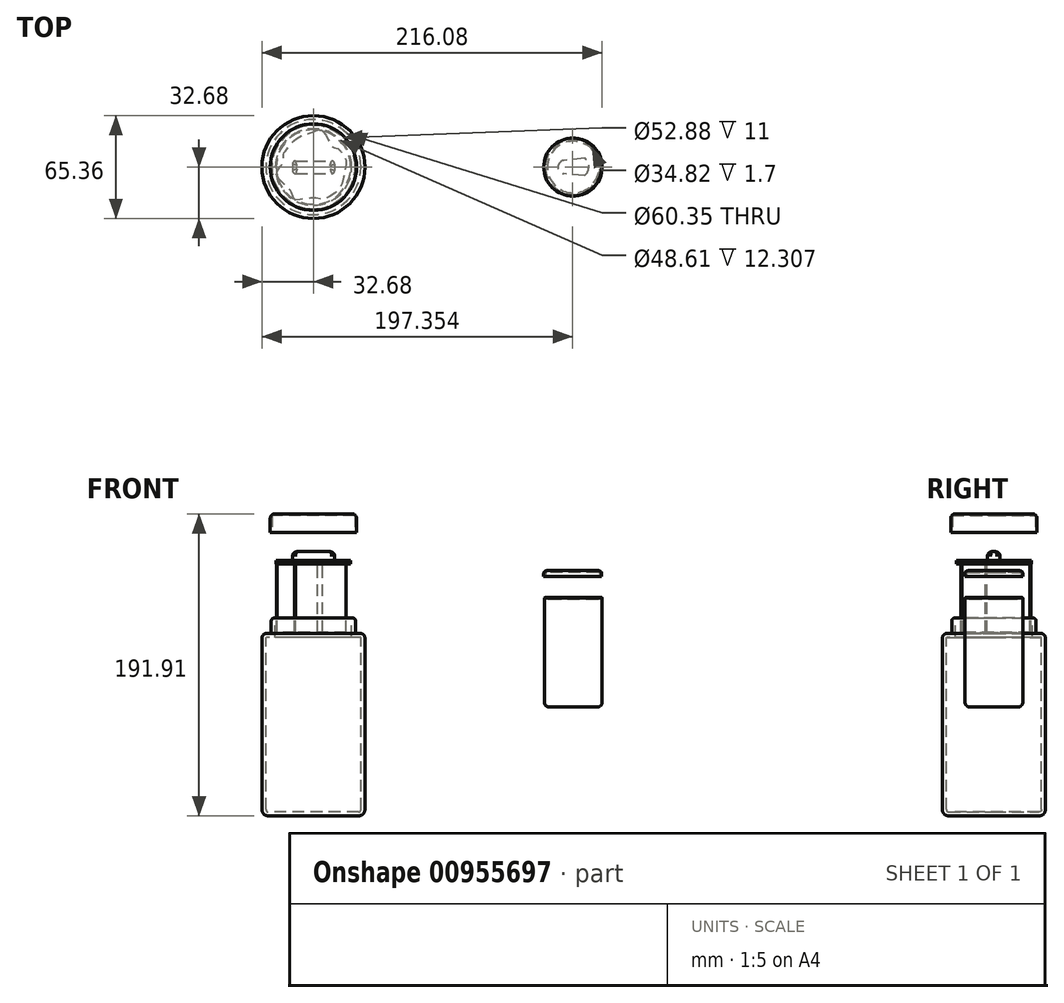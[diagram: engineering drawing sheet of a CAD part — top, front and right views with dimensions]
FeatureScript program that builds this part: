
annotation { "Feature Type Name" : "Feature", "Feature Type Description" : "" }
export const myFeature = defineFeature(function(context is Context, id is Id, definition is map)
    precondition{}
    {
        {
            var Q0;
            Q0=qCreatedBy(makeId("Front.planeOp"),FACE);
            var sketch = newSketch(context, id + "F0", { "sketchPlane" : qUnion([Q0])});
            skLineSegment(sketch, "E0", {"start": v(0, 62.51) * mm, "end": v(0, -116.4) * mm});
            skLineSegment(sketch, "E1", {"start": v(0, 58.07) * mm, "end": v(24.8, 58.07) * mm});
            skLineSegment(sketch, "E2", {"start": v(26.8, 56.07) * mm, "end": v(26.8, 48.27) * mm});
            skLineSegment(sketch, "E3", {"start": v(26.8, 48.27) * mm, "end": v(29.68, 48.27) * mm});
            skLineSegment(sketch, "E4", {"start": v(32.68, 45.27) * mm, "end": v(32.68, -63.64) * mm});
            skLineSegment(sketch, "E5", {"start": v(28.68, -67.64) * mm, "end": v(0, -67.64) * mm});
            skPoint(sketch, "E6.visualSharp", {"position": v(32.68, 48.27) * mm});
            skArc(sketch, "E6.filletArc", {"start": v(32.68, 45.27) * mm, "mid": v(31.8, 47.39) * mm, "end": v(29.68, 48.27) * mm});
            skPoint(sketch, "E7.visualSharp", {"position": v(32.68, -67.64) * mm});
            skArc(sketch, "E7.filletArc", {"start": v(28.68, -67.64) * mm, "mid": v(31.5, -66.47) * mm, "end": v(32.68, -63.64) * mm});
            skPoint(sketch, "E8.visualSharp", {"position": v(26.8, 58.07) * mm});
            skArc(sketch, "E8.filletArc", {"start": v(26.8, 56.07) * mm, "mid": v(26.22, 57.49) * mm, "end": v(24.8, 58.07) * mm});
            skSolve(sketch);
        }
        {
            var Q0;
            {var subQ0=sQuery(id+"F0.wireOp",EDGE,"E1");Q0=makeQuery(id+"F0.imprint","IMPRINT",FACE,{"disambiguationData":[TD([[makeQuery(id+"F0.imprint","IMPRINT",EDGE,{"derivedFrom":subQ0}),-1.0]])]});}
            var Q1;
            Q1=sQuery(id+"F0.wireOp",EDGE,"E0");
            revolve(context, id + "F1", {"surfaceOperationType" : NewSurfaceOperationType.NEW, "entities" : qUnion([Q0]), "axis" : qUnion([Q1]), "revolveType" : RevolveType.FULL});
        }
        {
            var Q0;
            Q0=makeQuery(id+"F1.opRevolve","SWEPT_FACE",FACE,{"disambiguationData":[OSD([sQuery(id+"F0.wireOp",EDGE,"E1")])]});
            shell(context, id + "F2", {"entities" : qUnion([Q0]), "thickness" : 2.5 * mm});
        }
        {
            var Q0;
            Q0=makeQuery(id+"F1.opRevolve","SWEPT_FACE",FACE,{"disambiguationData":[OSD([sQuery(id+"F0.wireOp",EDGE,"E3")])]});
            cPlane(context, id + "F3", {"entities" : qUnion([Q0]), "cplaneType" : CPlaneType.OFFSET, "offset" : 64 * mm, "width" : 150 * mm, "height" : 150 * mm});
        }
        {
            var Q0;
            Q0=qCreatedBy(id+"F3.planeOp",FACE);
            var sketch = newSketch(context, id + "F4", { "sketchPlane" : qUnion([Q0])});
            skCircle(sketch, "E9", {"center": v(0, 0) * mm, "radius": 27.44 * mm});
            skSolve(sketch);
        }
        {
            var Q0;
            Q0=makeQuery(id+"F4.imprint","IMPRINT",FACE,{"disambiguationData":[TD([[makeQuery(id+"F4.imprint","IMPRINT",EDGE,{"derivedFrom":sQuery(id+"F4.wireOp",EDGE,"E9")}),1.0]])]});
            extrude(context, id + "F5", {"entities" : qUnion([Q0]), "depth" : 12 * mm, "offsetDistance" : 25 * mm});
        }
        {
            var Q0;
            Q0=makeQuery(id+"F5.opExtrude","CAP_FACE",FACE,{"disambiguationData":[OSD([sQuery(id+"F4.wireOp",EDGE,"E9")])],"isStart":true});
            shell(context, id + "F6", {"entities" : qUnion([Q0]), "thickness" : 1 * mm});
        }
        {
            var Q0;
            Q0=qCreatedBy(id+"F3.planeOp",FACE);
            cPlane(context, id + "F7", {"entities" : qUnion([Q0]), "cplaneType" : CPlaneType.OFFSET, "offset" : 20 * mm, "oppositeDirection" : true, "width" : 150 * mm, "height" : 150 * mm});
        }
        {
            var Q0;
            Q0=qCreatedBy(id+"F7.planeOp",FACE);
            var sketch = newSketch(context, id + "F8", { "sketchPlane" : qUnion([Q0])});
            skCircle(sketch, "E10", {"center": v(0, 0) * mm, "radius": 23.67 * mm});
            skSolve(sketch);
        }
        {
            var Q0;
            Q0=makeQuery(id+"F8.imprint","IMPRINT",FACE,{"disambiguationData":[TD([[makeQuery(id+"F8.imprint","IMPRINT",EDGE,{"derivedFrom":sQuery(id+"F8.wireOp",EDGE,"E10")}),1.0]])]});
            extrude(context, id + "F9", {"entities" : qUnion([Q0]), "depth" : 2.4 * mm, "offsetDistance" : 25 * mm});
        }
        {
            var Q0;
            Q0=makeQuery(id+"F9.opExtrude","CAP_FACE",FACE,{"disambiguationData":[OSD([sQuery(id+"F8.wireOp",EDGE,"E10")])],"isStart":false});
            var sketch = newSketch(context, id + "F10", { "sketchPlane" : qUnion([Q0])});
            skLineSegment(sketch, "E11.bottom", {"start": v(-11.34, 3.9) * mm, "end": v(11.52, 3.9) * mm});
            skLineSegment(sketch, "E11.top", {"start": v(-11.34, -4.08) * mm, "end": v(11.52, -4.08) * mm});
            skLineSegment(sketch, "E11.left", {"start": v(-13.34, 1.9) * mm, "end": v(-13.34, -2.08) * mm});
            skLineSegment(sketch, "E11.right", {"start": v(13.52, 1.9) * mm, "end": v(13.52, -2.08) * mm});
            skPoint(sketch, "E12.visualSharp", {"position": v(-13.34, -4.08) * mm});
            skArc(sketch, "E12.filletArc", {"start": v(-13.34, -2.08) * mm, "mid": v(-12.75, -3.5) * mm, "end": v(-11.34, -4.08) * mm});
            skPoint(sketch, "E13.visualSharp", {"position": v(13.52, 3.9) * mm});
            skArc(sketch, "E13.filletArc", {"start": v(13.52, 1.9) * mm, "mid": v(12.93, 3.32) * mm, "end": v(11.52, 3.9) * mm});
            skPoint(sketch, "E14.visualSharp", {"position": v(13.52, -4.08) * mm});
            skArc(sketch, "E14.filletArc", {"start": v(11.52, -4.08) * mm, "mid": v(12.93, -3.5) * mm, "end": v(13.52, -2.08) * mm});
            skPoint(sketch, "E15.visualSharp", {"position": v(-13.34, 3.9) * mm});
            skArc(sketch, "E15.filletArc", {"start": v(-11.34, 3.9) * mm, "mid": v(-12.75, 3.32) * mm, "end": v(-13.34, 1.9) * mm});
            skSolve(sketch);
        }
        {
            var Q0;
            Q0=makeQuery(id+"F10.imprint","IMPRINT",FACE,{"disambiguationData":[TD([[makeQuery(id+"F10.imprint","IMPRINT",EDGE,{"derivedFrom":sQuery(id+"F10.wireOp",EDGE,"E11.bottom")}),-1.0]])]});
            extrude(context, id + "F11", {"entities" : qUnion([Q0]), "operationType" : NewBodyOperationType.ADD, "depth" : 5.5 * mm, "offsetDistance" : 25 * mm});
        }
        {
            var Q0;
            Q0=makeQuery(id+"F11.opExtrude","CAP_EDGE",EDGE,{"disambiguationData":[OSD([sQuery(id+"F10.wireOp",EDGE,"E11.top")])],"isStart":false});
            var Q1;
            Q1=makeQuery(id+"F11.opExtrude","CAP_EDGE",EDGE,{"disambiguationData":[OSD([sQuery(id+"F10.wireOp",EDGE,"E11.bottom")])],"isStart":false});
            var Q2;
            Q2=makeQuery(id+"F11.opExtrude","CAP_EDGE",EDGE,{"disambiguationData":[OSD([sQuery(id+"F10.wireOp",EDGE,"E11.right")])],"isStart":false});
            var Q3;
            Q3=makeQuery(id+"F11.opExtrude","CAP_EDGE",EDGE,{"disambiguationData":[OSD([sQuery(id+"F10.wireOp",EDGE,"E14.filletArc")])],"isStart":false});
            var Q4;
            Q4=makeQuery(id+"F11.opExtrude","CAP_EDGE",EDGE,{"disambiguationData":[OSD([sQuery(id+"F10.wireOp",EDGE,"E12.filletArc")])],"isStart":false});
            var Q5;
            Q5=makeQuery(id+"F11.opExtrude","CAP_EDGE",EDGE,{"disambiguationData":[OSD([sQuery(id+"F10.wireOp",EDGE,"E11.left")])],"isStart":false});
            var Q6;
            Q6=makeQuery(id+"F11.opExtrude","CAP_EDGE",EDGE,{"disambiguationData":[OSD([sQuery(id+"F10.wireOp",EDGE,"E15.filletArc")])],"isStart":false});
            fillet(context, id + "F12", {"entities" : qUnion([Q0, Q1, Q2, Q3, Q4, Q5, Q6]), "radius" : 2.9 * mm, "tangentPropagation" : true, "allowEdgeOverflow" : false});
        }
        {
            var Q0;
            Q0=makeQuery(id+"F9.opExtrude","CAP_FACE",FACE,{"disambiguationData":[OSD([sQuery(id+"F8.wireOp",EDGE,"E10")])],"isStart":true});
            var sketch = newSketch(context, id + "F13", { "sketchPlane" : qUnion([Q0])});
            skFitSpline(sketch, "E16", {"points": [v(19.77, 3.16) * mm, v(17.53, 12.36) * mm, v(12.33, 17.34) * mm, v(6.35, 20.4) * mm, v(3.03, 19.97) * mm, v(-2.59, 19.85) * mm, v(-8.58, 20.69) * mm, v(-11.97, 20.42) * mm, v(-14.47, 15.07) * mm, v(-18.87, 10.66) * mm, v(-23.23, 4.53) * mm, v(-21.38, 0) * mm, v(-19.28, -3.24) * mm, v(-18.87, -8.54) * mm, v(-17.35, -10.77) * mm, v(-11.99, -17.04) * mm, v(-6.84, -20.2) * mm, v(0, -22.42) * mm, v(2.7, -23.52) * mm, v(5.9, -22.93) * mm, v(8.87, -18.27) * mm, v(10.13, -16.18) * mm, v(11.58, -13.17) * mm, v(13.5, -12.2) * mm, v(16.52, -11) * mm, v(19.4, -6.9) * mm, v(20.84, -3.27) * mm, v(19.77, 3.16) * mm]});
            skSolve(sketch);
        }
        {
            var Q0;
            {var subQ0=sQuery(id+"F13.wireOp",EDGE,"E16");var subQ1=makeQuery(id+"F9.opExtrude","CAP_EDGE",EDGE,{"disambiguationData":[OSD([sQuery(id+"F8.wireOp",EDGE,"E10")])],"isStart":true});var subQ2=makeQuery(id+"F13.imprint","INTERSECT",VERTEX,{"disambiguationData":[OD(0.0)],"derivedFrom":[subQ1,subQ0]});Q0=makeQuery(id+"F13.imprint","IMPRINT",FACE,{"disambiguationData":[TD([[makeQuery(id+"F13.imprint","IMPRINT",EDGE,{"disambiguationData":[TD([[subQ2,-1.0]])],"derivedFrom":subQ0}),1.0]])]});}
            extrude(context, id + "F14", {"entities" : qUnion([Q0]), "depth" : 43.3 * mm, "offsetDistance" : 25 * mm});
        }
        {
            var Q0;
            Q0=makeQuery(id+"F5.opExtrude","CAP_EDGE",EDGE,{"disambiguationData":[OSD([sQuery(id+"F4.wireOp",EDGE,"E9")])],"isStart":false});
            fillet(context, id + "F15", {"entities" : qUnion([Q0]), "radius" : 3 * mm, "tangentPropagation" : true, "allowEdgeOverflow" : false});
        }
        {
            var Q0;
            Q0=qCreatedBy(makeId("Front.planeOp"),FACE);
            var sketch = newSketch(context, id + "F16", { "sketchPlane" : qUnion([Q0])});
            skLineSegment(sketch, "E17", {"start": v(165.05, 79.94) * mm, "end": v(165.05, -91.82) * mm});
            skLineSegment(sketch, "E18", {"start": v(165.05, 70.8) * mm, "end": v(151.78, 70.8) * mm});
            skArc(sketch, "E19", {"start": v(148.63, 70.8) * mm, "mid": v(149.76, 70.02) * mm, "end": v(151.05, 70.48) * mm});
            skLineSegment(sketch, "E20", {"start": v(146.7, 70.8) * mm, "end": v(146.7, 4.55) * mm});
            skLineSegment(sketch, "E21", {"start": v(149.7, 1.55) * mm, "end": v(165.05, 1.55) * mm});
            skPoint(sketch, "E22.visualSharp", {"position": v(146.7, 1.55) * mm});
            skArc(sketch, "E22.filletArc", {"start": v(146.7, 4.55) * mm, "mid": v(147.57, 2.42) * mm, "end": v(149.7, 1.55) * mm});
            skPoint(sketch, "E23.visualSharp", {"position": v(151.28, 70.8) * mm});
            skArc(sketch, "E23.filletArc", {"start": v(151.78, 70.8) * mm, "mid": v(151.38, 70.71) * mm, "end": v(151.05, 70.48) * mm});
            skArc(sketch, "E24", {"start": v(148.63, 70.8) * mm, "mid": v(147.66, 71.16) * mm, "end": v(146.7, 70.8) * mm});
            skSolve(sketch);
        }
        {
            var Q0;
            {var subQ0=sQuery(id+"F16.wireOp",EDGE,"E18");Q0=makeQuery(id+"F16.imprint","IMPRINT",FACE,{"disambiguationData":[TD([[makeQuery(id+"F16.imprint","IMPRINT",EDGE,{"derivedFrom":subQ0}),1.0]])]});}
            var Q1;
            Q1=sQuery(id+"F16.wireOp",EDGE,"E17");
            revolve(context, id + "F17", {"surfaceOperationType" : NewSurfaceOperationType.NEW, "entities" : qUnion([Q0]), "axis" : qUnion([Q1]), "revolveType" : RevolveType.FULL});
        }
        {
            var Q0;
            Q0=makeQuery(id+"F17.opRevolve","SWEPT_FACE",FACE,{"disambiguationData":[OSD([sQuery(id+"F16.wireOp",EDGE,"E18")])]});
            var sketch = newSketch(context, id + "F18", { "sketchPlane" : qUnion([Q0])});
            skArc(sketch, "E25", {"start": v(159.22, 4.28) * mm, "mid": v(155.36, -0.32) * mm, "end": v(159.86, -4.3) * mm});
            skArc(sketch, "E26", {"start": v(172.04, -5.42) * mm, "mid": v(174.92, 0.08) * mm, "end": v(172.36, 5.74) * mm});
            skLineSegment(sketch, "E27", {"start": v(172.36, 5.74) * mm, "end": v(159.13, 4.27) * mm});
            skLineSegment(sketch, "E28", {"start": v(172.04, -5.42) * mm, "end": v(158.67, -4.19) * mm});
            skSolve(sketch);
        }
        {
            var Q0;
            {var subQ4=sQuery(id+"F18.wireOp",EDGE,"E26");Q0=makeQuery(id+"F18.imprint","IMPRINT",FACE,{"disambiguationData":[TD([[makeQuery(id+"F18.imprint","IMPRINT",EDGE,{"derivedFrom":subQ4}),1.0]])]});}
            extrude(context, id + "F19", {"entities" : qUnion([Q0]), "operationType" : NewBodyOperationType.ADD, "depth" : .2 * mm, "offsetDistance" : 25 * mm});
        }
        {
            var Q0;
            Q0=makeQuery(id+"F17.opRevolve","SWEPT_FACE",FACE,{"disambiguationData":[OSD([sQuery(id+"F16.wireOp",EDGE,"E18")])]});
            cPlane(context, id + "F20", {"entities" : qUnion([Q0]), "cplaneType" : CPlaneType.OFFSET, "offset" : 13.6 * mm, "width" : 150 * mm, "height" : 150 * mm});
        }
        {
            var Q0;
            Q0=qCreatedBy(id+"F20.planeOp",FACE);
            var sketch = newSketch(context, id + "F21", { "sketchPlane" : qUnion([Q0])});
            skCircle(sketch, "E29", {"center": v(164.67, 0) * mm, "radius": 18.41 * mm});
            skSolve(sketch);
        }
        {
            var Q0;
            Q0=makeQuery(id+"F21.imprint","IMPRINT",FACE,{"disambiguationData":[TD([[makeQuery(id+"F21.imprint","IMPRINT",EDGE,{"derivedFrom":sQuery(id+"F21.wireOp",EDGE,"E29")}),1.0]])]});
            extrude(context, id + "F22", {"entities" : qUnion([Q0]), "depth" : 3.7 * mm, "offsetDistance" : 25 * mm});
        }
        {
            var Q0;
            Q0=makeQuery(id+"F22.opExtrude","CAP_EDGE",EDGE,{"disambiguationData":[OSD([sQuery(id+"F21.wireOp",EDGE,"E29")])],"isStart":false});
            fillet(context, id + "F23", {"entities" : qUnion([Q0]), "radius" : 2 * mm, "tangentPropagation" : true, "allowEdgeOverflow" : false});
        }
        {
            var Q0;
            Q0=makeQuery(id+"F22.opExtrude","CAP_FACE",FACE,{"disambiguationData":[OSD([sQuery(id+"F21.wireOp",EDGE,"E29")])],"isStart":true});
            shell(context, id + "F24", {"entities" : qUnion([Q0]), "thickness" : 1 * mm});
        }
    });
